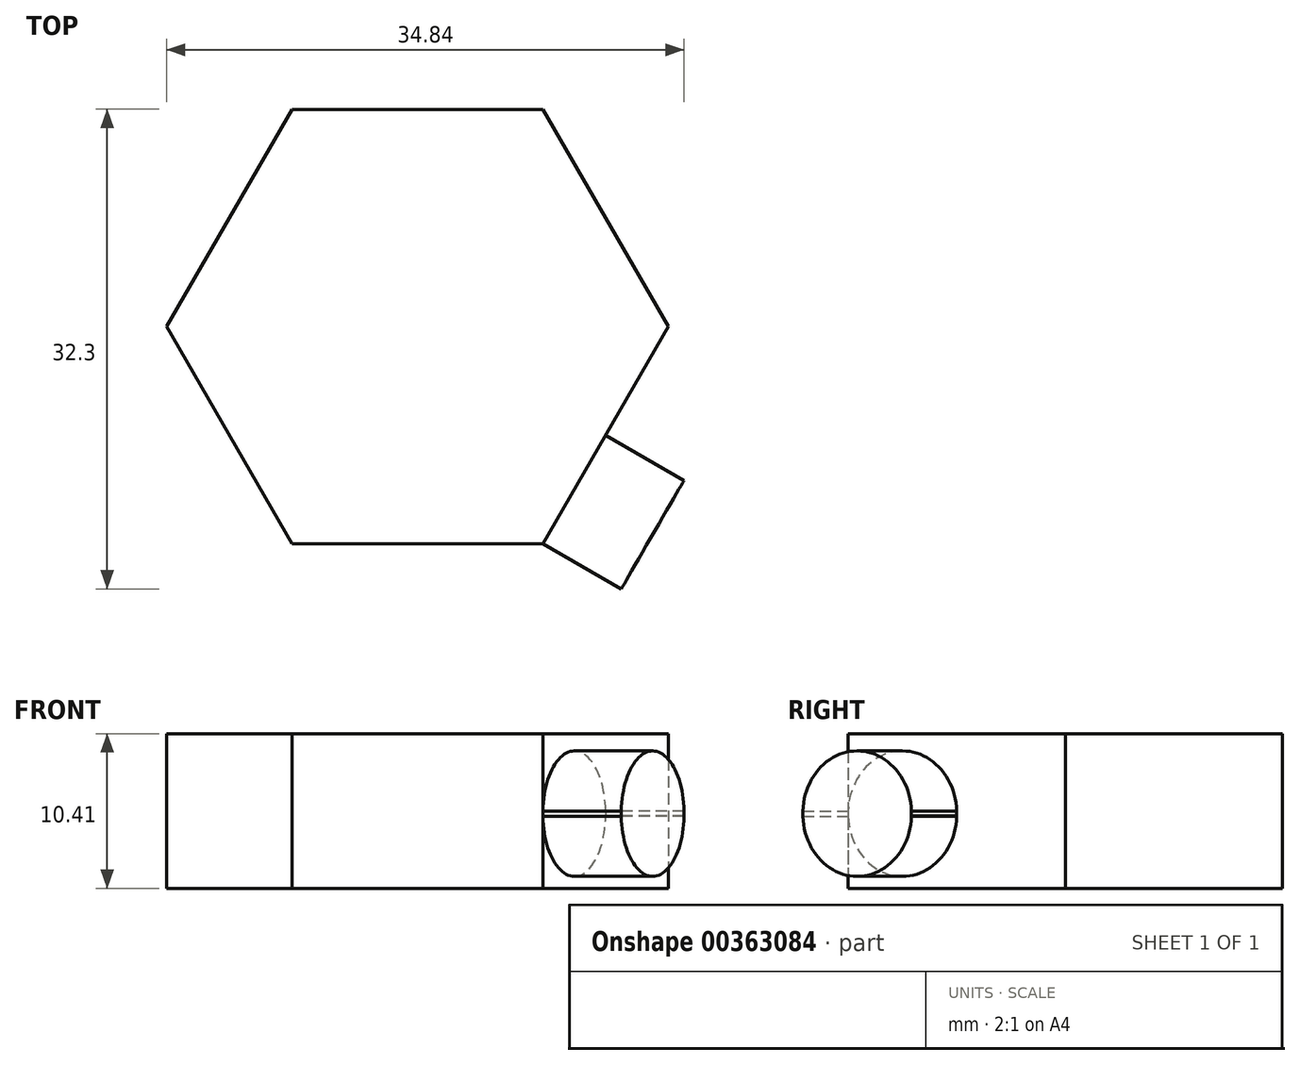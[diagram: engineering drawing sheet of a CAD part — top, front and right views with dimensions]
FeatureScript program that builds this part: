
annotation { "Feature Type Name" : "Feature", "Feature Type Description" : "" }
export const myFeature = defineFeature(function(context is Context, id is Id, definition is map)
    precondition{}
    {
        {
            var Q0;
            Q0=qCreatedBy(makeId("Top.planeOp"),FACE);
            var sketch = newSketch(context, id + "F0", { "sketchPlane" : qUnion([Q0])});
            skCircle(sketch, "E0.cCircle", {"center": v(0, 0) * mm, "radius": 14.63 * mm, "construction": true});
            skLineSegment(sketch, "E0.0", {"start": v(-8.44, 14.63) * mm, "end": v(8.44, 14.63) * mm});
            skLineSegment(sketch, "E0.1", {"start": v(8.44, 14.63) * mm, "end": v(16.89, 0) * mm});
            skLineSegment(sketch, "E0.2", {"start": v(16.89, 0) * mm, "end": v(8.44, -14.63) * mm});
            skLineSegment(sketch, "E0.3", {"start": v(8.44, -14.63) * mm, "end": v(-8.44, -14.63) * mm});
            skLineSegment(sketch, "E0.4", {"start": v(-8.44, -14.63) * mm, "end": v(-16.89, 0) * mm});
            skLineSegment(sketch, "E0.5", {"start": v(-16.89, 0) * mm, "end": v(-8.44, 14.63) * mm});
            skPoint(sketch, "E0.0.midPoint", {"position": v(0, 14.63) * mm});
            skSolve(sketch);
        }
        {
            var Q0;
            Q0 = qSketchRegion(id + "F0", true);
            extrude(context, id + "F1", {"entities" : qUnion([Q0]), "depth" : 10.4 * mm});
        }
        {
            var Q0;
            Q0=makeQuery(id+"F1.opExtrude","SWEPT_FACE",FACE,{"disambiguationData":[OSD([sQuery(id+"F0.wireOp",EDGE,"E0.2")])]});
            var sketch = newSketch(context, id + "F2", { "sketchPlane" : qUnion([Q0])});
            skLineSegment(sketch, "E1.bottom", {"start": v(-8.44, 10.41) * mm, "end": v(0, 10.41) * mm});
            skLineSegment(sketch, "E1.top", {"start": v(-8.44, 0) * mm, "end": v(0, 0) * mm});
            skLineSegment(sketch, "E1.left", {"start": v(-8.44, 10.41) * mm, "end": v(-8.44, 0) * mm});
            skLineSegment(sketch, "E1.right", {"start": v(0, 10.41) * mm, "end": v(0, 0) * mm});
            skLineSegment(sketch, "E2.bottom", {"start": v(0, 10.41) * mm, "end": v(8.44, 10.41) * mm});
            skLineSegment(sketch, "E2.top", {"start": v(0, 0) * mm, "end": v(8.44, 0) * mm});
            skLineSegment(sketch, "E2.right", {"start": v(8.44, 10.41) * mm, "end": v(8.44, 0) * mm});
            skCircle(sketch, "E3", {"center": v(-4.22, 5.03) * mm, "radius": 4.23 * mm});
            skPoint(sketch, "E3.first.point", {"position": v(-8.44, 5.2) * mm});
            skPoint(sketch, "E3.second.point", {"position": v(0, 5.2) * mm});
            skPoint(sketch, "E3.third.point", {"position": v(-4.22, 9.25) * mm});
            skPoint(sketch, "E3.third.point.positionSnap0", {"position": v(-4.22, 10.41) * mm});
            skCircle(sketch, "E4", {"center": v(4.22, 5.04) * mm, "radius": 4.23 * mm});
            skPoint(sketch, "E4.second.point", {"position": v(8.44, 5.2) * mm});
            skPoint(sketch, "E4.third.point", {"position": v(3.94, 9.25) * mm});
            skSolve(sketch);
        }
        {
            var Q0;
            {var subQ0=sQuery(id+"F2.wireOp",EDGE,"E3");var subQ1=sQuery(id+"F2.wireOp",EDGE,"E1.left");var subQ5=makeQuery(id+"F2.imprint","INTERSECT",VERTEX,{"disambiguationData":[OD(0.0)],"derivedFrom":[subQ1,subQ0]});Q0=makeQuery(id+"F2.imprint","IMPRINT",FACE,{"disambiguationData":[TD([[makeQuery(id+"F2.imprint","IMPRINT",EDGE,{"disambiguationData":[TD([[subQ5,-1.0]])],"derivedFrom":subQ1}),1.0]])]});}
            extrude(context, id + "F3", {"entities" : qUnion([Q0]), "operationType" : NewBodyOperationType.ADD, "depth" : 6.1 * mm});
        }
    });
